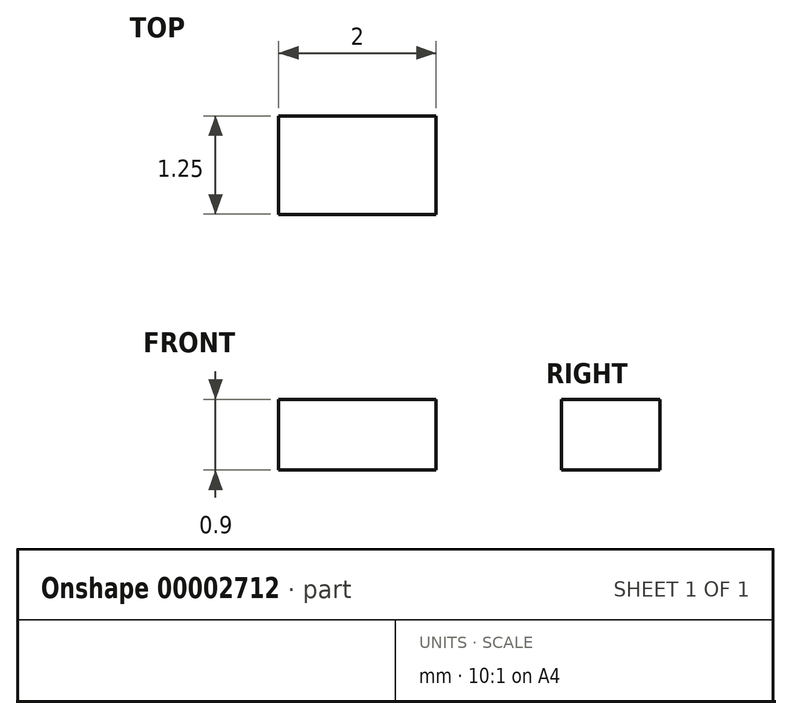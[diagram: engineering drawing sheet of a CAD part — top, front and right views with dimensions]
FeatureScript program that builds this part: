
annotation { "Feature Type Name" : "Feature", "Feature Type Description" : "" }
export const myFeature = defineFeature(function(context is Context, id is Id, definition is map)
    precondition{}
    {
        {
            var Q0;
            Q0=qCreatedBy(makeId("Top.planeOp"),FACE);
            var sketch = newSketch(context, id + "F0", { "sketchPlane" : qUnion([Q0])});
            skLineSegment(sketch, "E0.bottom", {"start": v(0.42, 1.2) * mm, "end": v(2.42, 1.2) * mm});
            skLineSegment(sketch, "E0.top", {"start": v(0.42, -0.04) * mm, "end": v(2.42, -0.04) * mm});
            skLineSegment(sketch, "E0.left", {"start": v(0.42, 1.2) * mm, "end": v(0.42, -0.04) * mm});
            skLineSegment(sketch, "E0.right", {"start": v(2.42, 1.2) * mm, "end": v(2.42, -0.04) * mm});
            skSolve(sketch);
        }
        {
            var Q0;
            Q0=makeQuery(id+"F0.imprint","IMPRINT",FACE,{"disambiguationData":[TD([[makeQuery(id+"F0.imprint","IMPRINT",EDGE,{"derivedFrom":sQuery(id+"F0.wireOp",EDGE,"E0.bottom")}),-1.0]])]});
            extrude(context, id + "F1", {"entities" : qUnion([Q0]), "depth" : .9 * mm});
        }
    });
